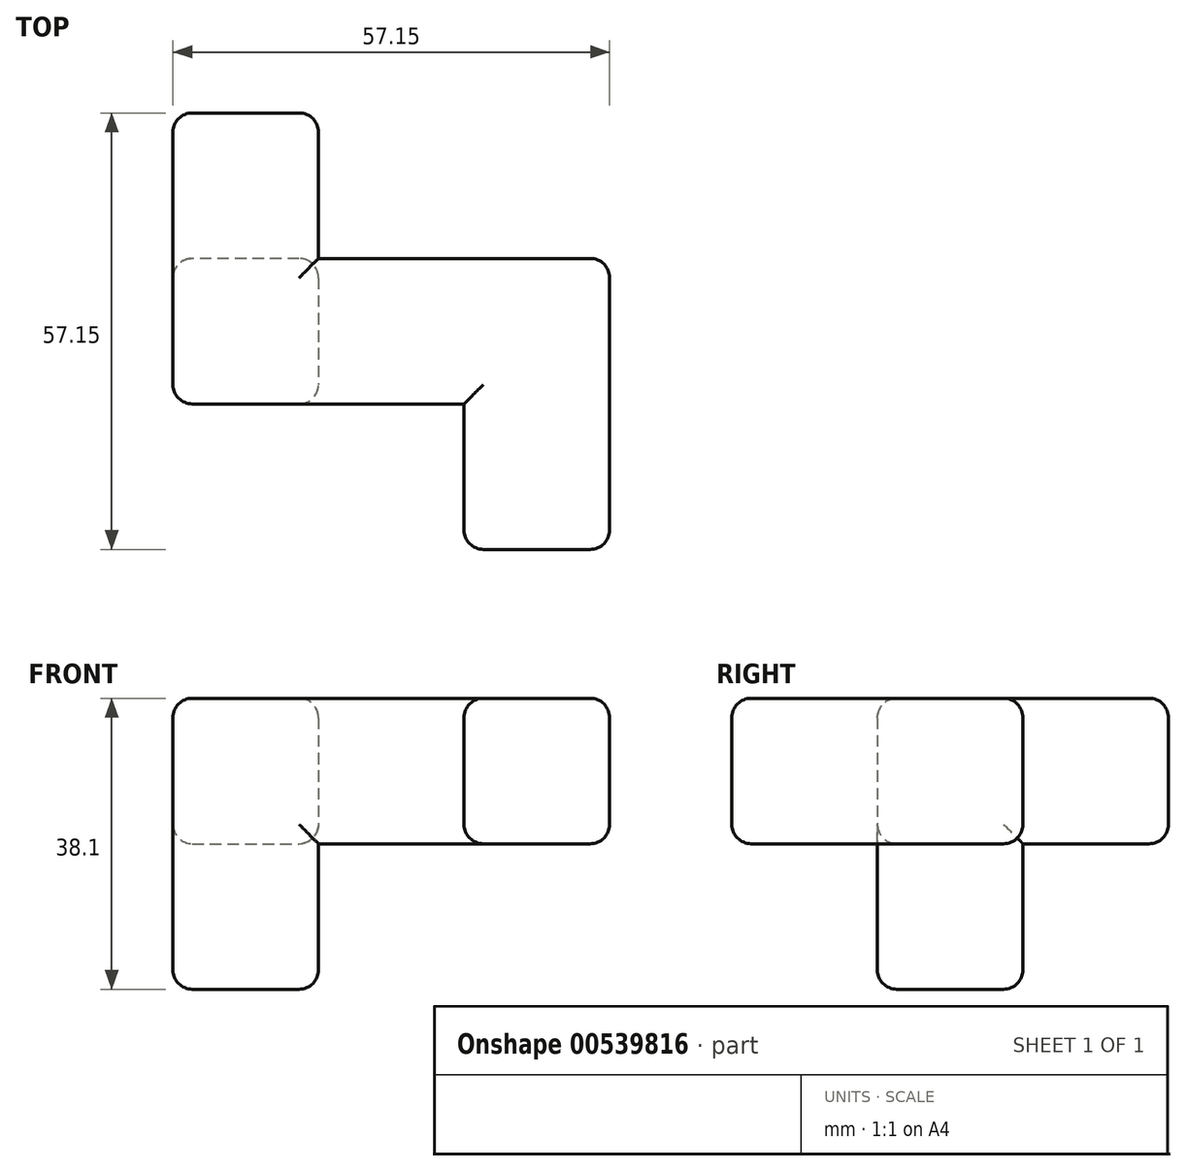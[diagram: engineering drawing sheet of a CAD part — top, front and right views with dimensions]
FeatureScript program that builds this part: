
annotation { "Feature Type Name" : "Feature", "Feature Type Description" : "" }
export const myFeature = defineFeature(function(context is Context, id is Id, definition is map)
    precondition{}
    {
        {
            var Q0;
            Q0=qCreatedBy(makeId("Top.planeOp"),FACE);
            var sketch = newSketch(context, id + "F0", { "sketchPlane" : qUnion([Q0])});
            skLineSegment(sketch, "E0", {"start": v(0, 0) * mm, "end": v(0, 38.1) * mm});
            skLineSegment(sketch, "E1", {"start": v(0, 38.1) * mm, "end": v(19.05, 38.1) * mm});
            skLineSegment(sketch, "E2", {"start": v(19.05, 38.1) * mm, "end": v(19.05, 19.05) * mm});
            skLineSegment(sketch, "E3", {"start": v(19.05, 19.05) * mm, "end": v(57.15, 19.05) * mm});
            skLineSegment(sketch, "E4", {"start": v(57.15, 19.05) * mm, "end": v(57.15, -19.05) * mm});
            skLineSegment(sketch, "E5", {"start": v(57.15, -19.05) * mm, "end": v(38.1, -19.05) * mm});
            skLineSegment(sketch, "E6", {"start": v(38.1, -19.05) * mm, "end": v(38.1, 0) * mm});
            skLineSegment(sketch, "E7", {"start": v(38.1, 0) * mm, "end": v(0, 0) * mm});
            skSolve(sketch);
        }
        {
            var Q0;
            Q0=makeQuery(id+"F0.imprint","IMPRINT",FACE,{"disambiguationData":[TD([[makeQuery(id+"F0.imprint","IMPRINT",EDGE,{"derivedFrom":sQuery(id+"F0.wireOp",EDGE,"E0")}),-1.0]])]});
            extrude(context, id + "F1", {"entities" : qUnion([Q0]), "depth" : 19.05 * mm, "offsetDistance" : 25.4 * mm});
        }
        {
            var Q0;
            Q0=makeQuery(id+"F1.opExtrude","CAP_FACE",FACE,{"disambiguationData":[OSD([sQuery(id+"F0.wireOp",EDGE,"E0"),sQuery(id+"F0.wireOp",EDGE,"E1"),sQuery(id+"F0.wireOp",EDGE,"E2"),sQuery(id+"F0.wireOp",EDGE,"E3"),sQuery(id+"F0.wireOp",EDGE,"E4"),sQuery(id+"F0.wireOp",EDGE,"E5"),sQuery(id+"F0.wireOp",EDGE,"E6"),sQuery(id+"F0.wireOp",EDGE,"E7")])],"isStart":true});
            var sketch = newSketch(context, id + "F2", { "sketchPlane" : qUnion([Q0])});
            skLineSegment(sketch, "E8.bottom", {"start": v(19.05, -19.05) * mm, "end": v(0, -19.05) * mm});
            skLineSegment(sketch, "E8.top", {"start": v(19.05, 0) * mm, "end": v(0, 0) * mm});
            skLineSegment(sketch, "E8.left", {"start": v(19.05, -19.05) * mm, "end": v(19.05, 0) * mm});
            skLineSegment(sketch, "E8.right", {"start": v(0, -19.05) * mm, "end": v(0, 0) * mm});
            skSolve(sketch);
        }
        {
            var Q0;
            Q0=makeQuery(id+"F2.imprint","IMPRINT",FACE,{"disambiguationData":[TD([[makeQuery(id+"F2.imprint","IMPRINT",EDGE,{"derivedFrom":sQuery(id+"F2.wireOp",EDGE,"E8.bottom")}),-1.0]])]});
            extrude(context, id + "F3", {"entities" : qUnion([Q0]), "operationType" : NewBodyOperationType.ADD, "depth" : 19.05 * mm, "offsetDistance" : 25.4 * mm});
        }
        {
            var Q0;
            Q0=makeQuery(id+"F1.opExtrude","CAP_FACE",FACE,{"disambiguationData":[OSD([sQuery(id+"F0.wireOp",EDGE,"E0"),sQuery(id+"F0.wireOp",EDGE,"E1"),sQuery(id+"F0.wireOp",EDGE,"E2"),sQuery(id+"F0.wireOp",EDGE,"E3"),sQuery(id+"F0.wireOp",EDGE,"E4"),sQuery(id+"F0.wireOp",EDGE,"E5"),sQuery(id+"F0.wireOp",EDGE,"E6"),sQuery(id+"F0.wireOp",EDGE,"E7")])],"isStart":false});
            var Q1;
            Q1=makeQuery(id+"F1.opExtrude","SWEPT_FACE",FACE,{"disambiguationData":[OSD([sQuery(id+"F0.wireOp",EDGE,"E4")])]});
            var Q2;
            Q2=makeQuery(id+"F1.opExtrude","SWEPT_FACE",FACE,{"disambiguationData":[OSD([sQuery(id+"F0.wireOp",EDGE,"E1")])]});
            var Q3;
            Q3=makeQuery(id+"F3.boolean.opBoolean","MERGE",FACE,{"derivedFrom":[makeQuery(id+"F1.opExtrude","SWEPT_FACE",FACE,{"disambiguationData":[OSD([sQuery(id+"F0.wireOp",EDGE,"E0")])]}),makeQuery(id+"F3.opExtrude","SWEPT_FACE",FACE,{"disambiguationData":[OSD([sQuery(id+"F2.wireOp",EDGE,"E8.right")])]})]});
            var Q4;
            Q4=makeQuery(id+"F1.opExtrude","SWEPT_FACE",FACE,{"disambiguationData":[OSD([sQuery(id+"F0.wireOp",EDGE,"E5")])]});
            var Q5;
            Q5=makeQuery(id+"F3.opExtrude","CAP_FACE",FACE,{"disambiguationData":[OSD([sQuery(id+"F2.wireOp",EDGE,"E8.bottom"),sQuery(id+"F2.wireOp",EDGE,"E8.top"),sQuery(id+"F2.wireOp",EDGE,"E8.left"),sQuery(id+"F2.wireOp",EDGE,"E8.right")])],"isStart":false});
            var Q6;
            Q6=makeQuery(id+"F1.opExtrude","CAP_EDGE",EDGE,{"disambiguationData":[OSD([sQuery(id+"F0.wireOp",EDGE,"E6")])],"isStart":true});
            var Q7;
            Q7=makeQuery(id+"F3.opExtrude","SWEPT_EDGE",EDGE,{"disambiguationData":[OSD([sQuery(id+"F0.wireOp",EDGE,"E7"),sQuery(id+"F2.wireOp",EDGE,"E8.top"),sQuery(id+"F2.wireOp",EDGE,"E8.left")])]});
            var Q8;
            Q8=makeQuery(id+"F1.opExtrude","CAP_EDGE",EDGE,{"disambiguationData":[OSD([sQuery(id+"F0.wireOp",EDGE,"E3")])],"isStart":true});
            fillet(context, id + "F4", {"entities" : qUnion([Q0, Q1, Q2, Q3, Q4, Q5, Q6, Q7, Q8]), "radius" : 2.54 * mm, "tangentPropagation" : true, "allowEdgeOverflow" : false});
        }
        {
            var Q0;
            Q0=makeQuery(id+"F1.opExtrude","CAP_EDGE",EDGE,{"disambiguationData":[OSD([sQuery(id+"F0.wireOp",EDGE,"E2")])],"isStart":true});
            var Q1;
            Q1=makeQuery(id+"F1.opExtrude","CAP_EDGE",EDGE,{"disambiguationData":[OSD([sQuery(id+"F0.wireOp",EDGE,"E7")])],"isStart":true});
            fillet(context, id + "F5", {"entities" : qUnion([Q0, Q1]), "radius" : 2.54 * mm, "tangentPropagation" : true, "allowEdgeOverflow" : false});
        }
        {
            var Q0;
            Q0=makeQuery(id+"F3.opExtrude","SWEPT_EDGE",EDGE,{"disambiguationData":[OSD([sQuery(id+"F0.wireOp",EDGE,"E2"),sQuery(id+"F0.wireOp",EDGE,"E3"),sQuery(id+"F2.wireOp",EDGE,"E8.bottom"),sQuery(id+"F2.wireOp",EDGE,"E8.left")])]});
            fillet(context, id + "F6", {"entities" : qUnion([Q0]), "radius" : 2.54 * mm, "tangentPropagation" : true, "allowEdgeOverflow" : false});
        }
    });
